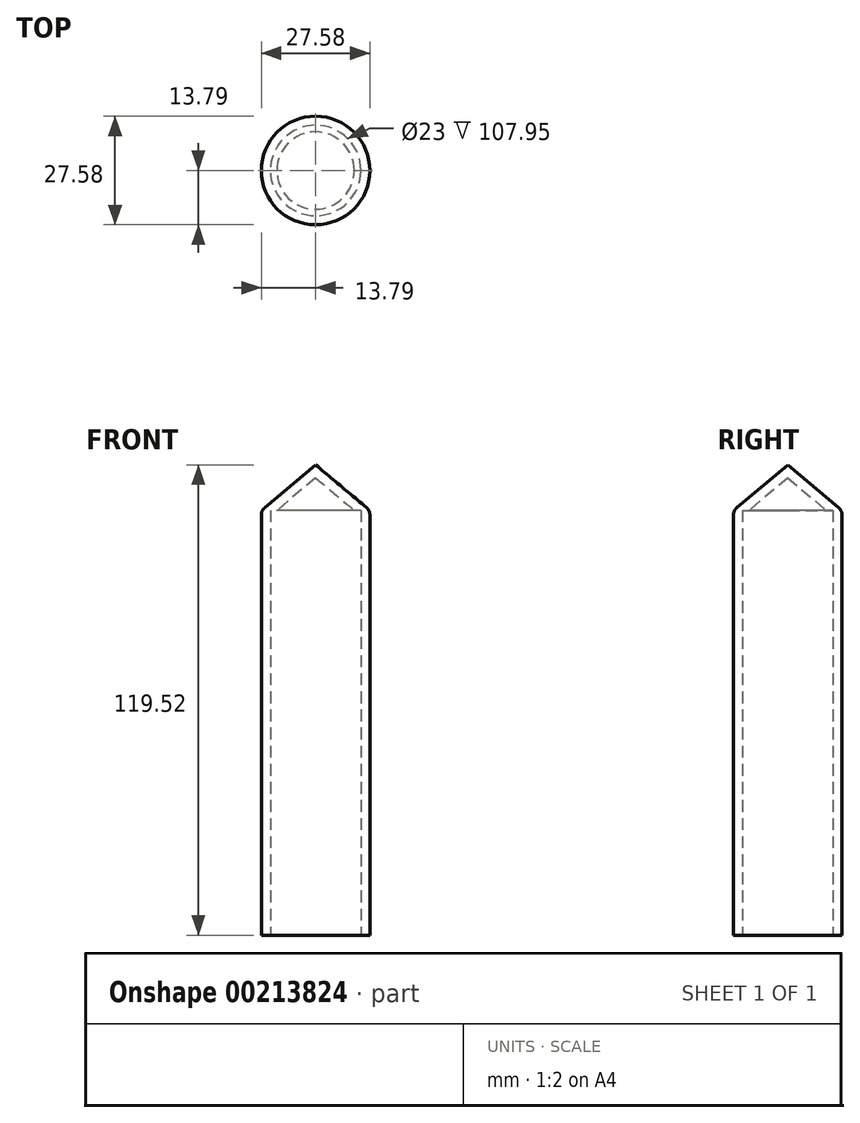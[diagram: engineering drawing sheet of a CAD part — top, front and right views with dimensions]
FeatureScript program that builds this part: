
annotation { "Feature Type Name" : "Feature", "Feature Type Description" : "" }
export const myFeature = defineFeature(function(context is Context, id is Id, definition is map)
    precondition{}
    {
        {
            var Q0;
            Q0=qCreatedBy(makeId("Top.planeOp"),FACE);
            var sketch = newSketch(context, id + "F0", { "sketchPlane" : qUnion([Q0])});
            skCircle(sketch, "E0", {"center": v(0, 0) * mm, "radius": 11.5 * mm});
            skCircle(sketch, "E1", {"center": v(0, 0) * mm, "radius": 13.79 * mm});
            skSolve(sketch);
        }
        {
            var Q0;
            Q0=makeQuery(id+"F0.imprint","IMPRINT",FACE,{"disambiguationData":[TD([[makeQuery(id+"F0.imprint","IMPRINT",EDGE,{"derivedFrom":sQuery(id+"F0.wireOp",EDGE,"E0")}),-1.0]])]});
            var Q1;
            Q1 = qSketchRegion(id + "F2", true);
            extrude(context, id + "F1", {"entities" : qUnion([Q0, Q1]), "depth" : 107.95 * mm});
        }
        {
            var Q0;
            Q0=makeQuery(id+"F1.opExtrude","CAP_FACE",FACE,{"disambiguationData":[OSD([sQuery(id+"F0.wireOp",EDGE,"E0"),sQuery(id+"F0.wireOp",EDGE,"E1")])],"isStart":false});
            var sketch = newSketch(context, id + "F2", { "sketchPlane" : qUnion([Q0])});
            skCircle(sketch, "E2.0", {"center": v(0, 0) * mm, "radius": 13.79 * mm});
            skSolve(sketch);
        }
        {
            var Q0;
            Q0=makeQuery(id+"F2.imprint","IMPRINT",FACE,{"disambiguationData":[TD([[makeQuery(id+"F2.imprint","IMPRINT",EDGE,{"derivedFrom":makeQuery(id+"F1.opExtrude","CAP_EDGE",EDGE,{"disambiguationData":[OSD([sQuery(id+"F0.wireOp",EDGE,"E0")])],"isStart":false})}),1.0]])]});
            var Q1;
            Q1=makeQuery(id+"F2.imprint","IMPRINT",FACE,{"disambiguationData":[TD([[makeQuery(id+"F2.imprint","IMPRINT",EDGE,{"derivedFrom":sQuery(id+"F2.wireOp",EDGE,"E2.0")}),1.0]])]});
            extrude(context, id + "F3", {"entities" : qUnion([Q0, Q1]), "operationType" : NewBodyOperationType.ADD, "depth" : 31.75 * mm, "hasDraft" : true, "draftAngle" : 50 * degree, "draftPullDirection" : true});
        }
        {
            var Q0;
            Q0=makeQuery(id+"F3.opExtrude","CAP_FACE",FACE,{"disambiguationData":[OSD([sQuery(id+"F2.wireOp",EDGE,"E2.0")])],"isStart":true});
            shell(context, id + "F4", {"entities" : qUnion([Q0]), "thickness" : 2.54 * mm});
        }
        {
            var Q0;
            Q0=makeQuery(id+"F1.opExtrude","SWEPT_BODY",BODY,{"disambiguationData":[OSD([sQuery(id+"F0.wireOp",EDGE,"E0"),sQuery(id+"F0.wireOp",EDGE,"E1")])]});
            var Q1;
            Q1=sQuery(id+"F0.wireOp",EDGE,"E1");
            circularPattern(context, id + "F5", {"entities" : qUnion([Q0]), "axis" : qUnion([Q1]), "angle" : 360 * degree, "instanceCount" : 4, "equalSpace" : true});
        }
        {
            var Q0;
            Q0=makeQuery(id+"F3.opExtrude","SWEPT_FACE",FACE,{"disambiguationData":[OSD([sQuery(id+"F2.wireOp",EDGE,"E2.0")])]});
            fillet(context, id + "F6", {"entities" : qUnion([Q0]), "radius" : 2.54 * mm, "tangentPropagation" : true, "allowEdgeOverflow" : false});
        }
        {
            var Q0;
            Q0=makeQuery(id+"F5.opPattern","COPY",BODY,{"derivedFrom":makeQuery(id+"F1.opExtrude","SWEPT_BODY",BODY,{"disambiguationData":[OSD([sQuery(id+"F0.wireOp",EDGE,"E0"),sQuery(id+"F0.wireOp",EDGE,"E1")])]}),"instanceName":"1"});
            deleteBodies(context, id + "F7", {"entities" : qUnion([Q0])});
        }
        {
            var Q0;
            Q0=makeQuery(id+"F5.opPattern","COPY",BODY,{"derivedFrom":makeQuery(id+"F1.opExtrude","SWEPT_BODY",BODY,{"disambiguationData":[OSD([sQuery(id+"F0.wireOp",EDGE,"E0"),sQuery(id+"F0.wireOp",EDGE,"E1")])]}),"instanceName":"3"});
            deleteBodies(context, id + "F8", {"entities" : qUnion([Q0])});
        }
        {
            var Q0;
            Q0=makeQuery(id+"F5.opPattern","COPY",BODY,{"derivedFrom":makeQuery(id+"F1.opExtrude","SWEPT_BODY",BODY,{"disambiguationData":[OSD([sQuery(id+"F0.wireOp",EDGE,"E0"),sQuery(id+"F0.wireOp",EDGE,"E1")])]}),"instanceName":"2"});
            deleteBodies(context, id + "F9", {"entities" : qUnion([Q0])});
        }
    });
